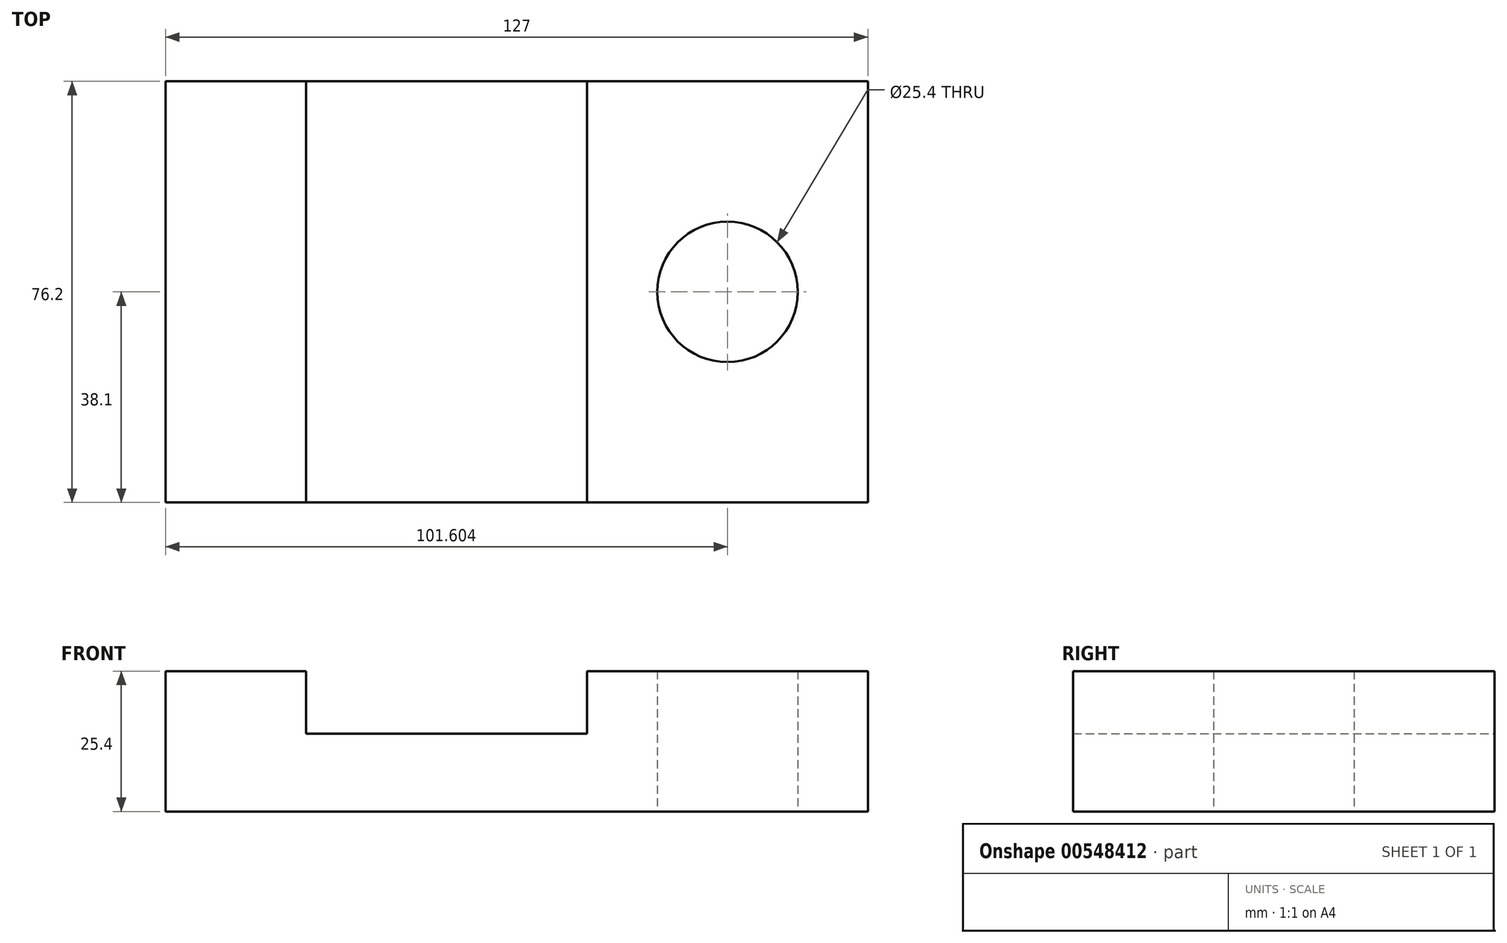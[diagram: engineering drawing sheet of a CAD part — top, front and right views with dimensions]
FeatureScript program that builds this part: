
annotation { "Feature Type Name" : "Feature", "Feature Type Description" : "" }
export const myFeature = defineFeature(function(context is Context, id is Id, definition is map)
    precondition{}
    {
        {
            var Q0;
            Q0=qCreatedBy(makeId("Front.planeOp"),FACE);
            var sketch = newSketch(context, id + "F0", { "sketchPlane" : qUnion([Q0])});
            skLineSegment(sketch, "E0", {"start": v(-40.53, 12.84) * mm, "end": v(-40.53, -12.56) * mm});
            skLineSegment(sketch, "E1", {"start": v(-40.53, -12.56) * mm, "end": v(86.47, -12.56) * mm});
            skLineSegment(sketch, "E2", {"start": v(-40.53, 12.84) * mm, "end": v(-15.13, 12.84) * mm});
            skLineSegment(sketch, "E3", {"start": v(-15.13, 12.84) * mm, "end": v(-15.13, 1.5) * mm});
            skLineSegment(sketch, "E4", {"start": v(-15.13, 1.5) * mm, "end": v(35.67, 1.5) * mm});
            skLineSegment(sketch, "E5", {"start": v(35.67, 1.5) * mm, "end": v(35.67, 12.84) * mm});
            skLineSegment(sketch, "E6", {"start": v(35.67, 12.84) * mm, "end": v(86.47, 12.84) * mm});
            skLineSegment(sketch, "E7", {"start": v(86.47, 12.84) * mm, "end": v(86.47, -12.56) * mm});
            skSolve(sketch);
        }
        {
            var Q0;
            Q0 = qSketchRegion(id + "F0", true);
            extrude(context, id + "F1", {"entities" : qUnion([Q0]), "depth" : 76.2 * mm, "offsetDistance" : 25.4 * mm});
        }
        {
            var Q0;
            Q0=qCreatedBy(makeId("Top.planeOp"),FACE);
            var sketch = newSketch(context, id + "F2", { "sketchPlane" : qUnion([Q0])});
            skCircle(sketch, "E8", {"center": v(61.07, -38.1) * mm, "radius": 12.7 * mm});
            skSolve(sketch);
        }
        {
            var Q0;
            Q0 = qSketchRegion(id + "F2", true);
            extrude(context, id + "F3", {"entities" : qUnion([Q0]), "operationType" : NewBodyOperationType.REMOVE, "depth" : 50.8 * mm, "offsetDistance" : 25.4 * mm});
        }
        {
            var Q0;
            Q0 = qSketchRegion(id + "F2", true);
            extrude(context, id + "F4", {"entities" : qUnion([Q0]), "operationType" : NewBodyOperationType.REMOVE, "oppositeDirection" : true, "depth" : 50.8 * mm, "offsetDistance" : 25.4 * mm});
        }
    });
